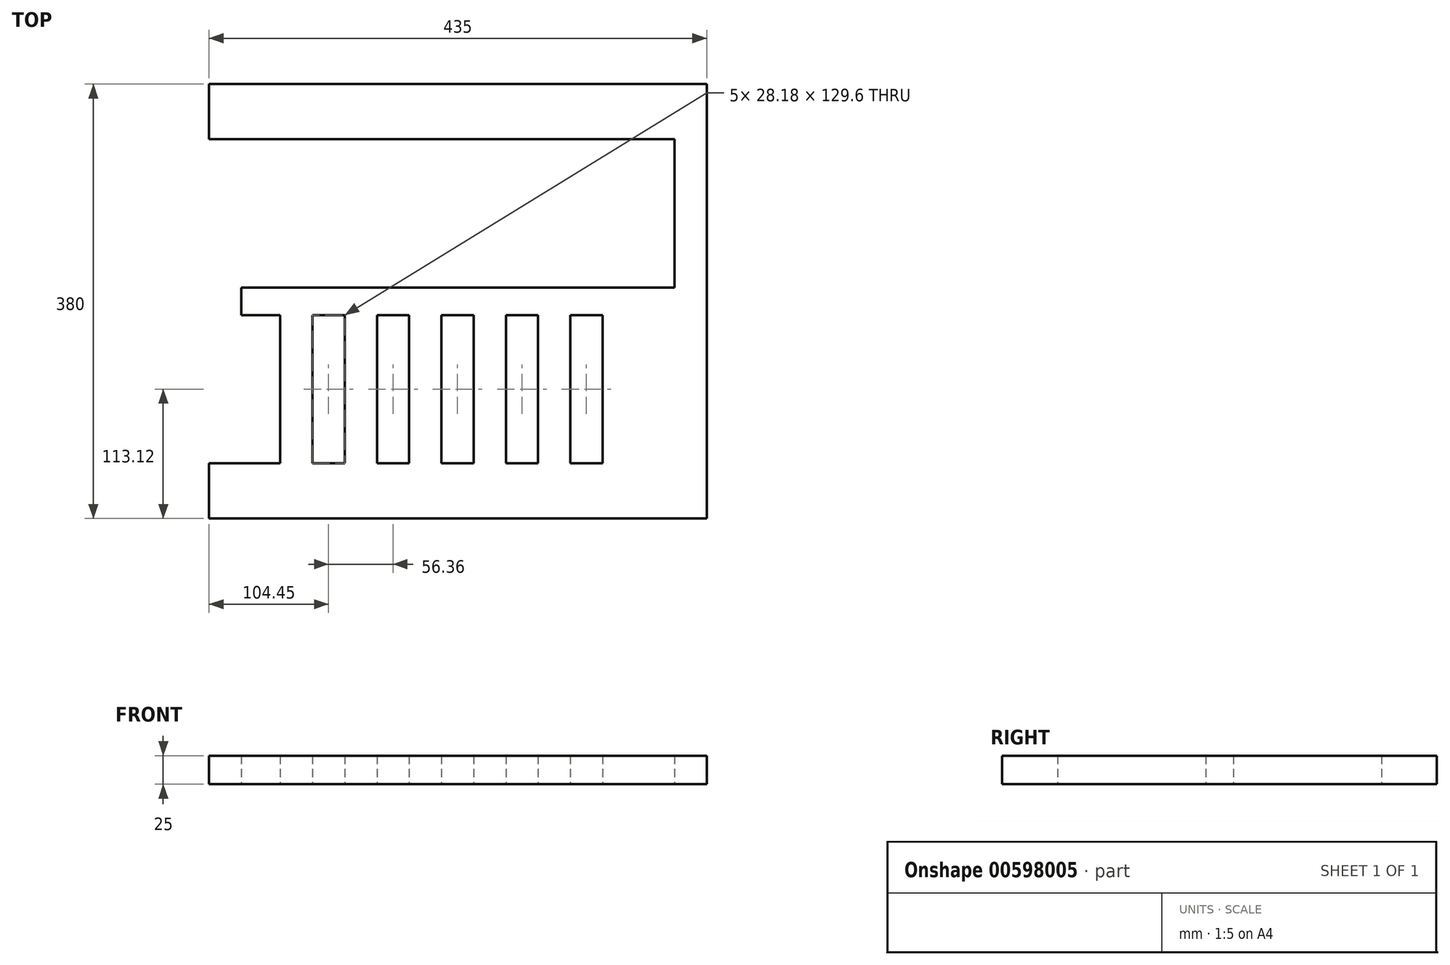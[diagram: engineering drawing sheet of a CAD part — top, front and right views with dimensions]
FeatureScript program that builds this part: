
annotation { "Feature Type Name" : "Feature", "Feature Type Description" : "" }
export const myFeature = defineFeature(function(context is Context, id is Id, definition is map)
    precondition{}
    {
        {
            var Q0;
            Q0=qCreatedBy(makeId("Top.planeOp"),FACE);
            var sketch = newSketch(context, id + "F0", { "sketchPlane" : qUnion([Q0])});
            skLineSegment(sketch, "E0.bottom", {"start": v(0, 0) * mm, "end": v(435, 0) * mm});
            skLineSegment(sketch, "E0.top", {"start": v(0, 380) * mm, "end": v(435, 380) * mm});
            skLineSegment(sketch, "E0.left", {"start": v(0, 0) * mm, "end": v(0, 380) * mm});
            skLineSegment(sketch, "E0.right", {"start": v(435, 0) * mm, "end": v(435, 380) * mm});
            skLineSegment(sketch, "E1", {"start": v(435, 0) * mm, "end": v(435, 48.32) * mm});
            skLineSegment(sketch, "E2", {"start": v(435, 380) * mm, "end": v(435, 331.68) * mm});
            skLineSegment(sketch, "E3.bottom", {"start": v(435, 331.68) * mm, "end": v(406.82, 331.68) * mm});
            skLineSegment(sketch, "E3.top", {"start": v(435, 48.32) * mm, "end": v(406.82, 48.32) * mm});
            skLineSegment(sketch, "E3.left", {"start": v(435, 331.68) * mm, "end": v(435, 48.32) * mm});
            skLineSegment(sketch, "E3.right", {"start": v(406.82, 331.68) * mm, "end": v(406.82, 48.32) * mm});
            skLineSegment(sketch, "E4", {"start": v(406.82, 331.68) * mm, "end": v(0, 331.68) * mm});
            skLineSegment(sketch, "E5", {"start": v(406.82, 48.32) * mm, "end": v(0, 48.32) * mm});
            skLineSegment(sketch, "E6.bottom", {"start": v(0, 331.68) * mm, "end": v(28.18, 331.68) * mm});
            skLineSegment(sketch, "E6.top", {"start": v(0, 48.32) * mm, "end": v(28.18, 48.32) * mm});
            skLineSegment(sketch, "E6.left", {"start": v(0, 331.68) * mm, "end": v(0, 48.32) * mm});
            skLineSegment(sketch, "E6.right", {"start": v(28.18, 331.68) * mm, "end": v(28.18, 48.32) * mm});
            skLineSegment(sketch, "E7", {"start": v(406.82, 48.32) * mm, "end": v(406.82, 177.92) * mm});
            skLineSegment(sketch, "E8", {"start": v(406.82, 331.68) * mm, "end": v(406.82, 202.08) * mm});
            skLineSegment(sketch, "E9", {"start": v(406.82, 202.08) * mm, "end": v(435, 202.08) * mm});
            skLineSegment(sketch, "E10", {"start": v(435, 177.75) * mm, "end": v(406.82, 177.92) * mm});
            skLineSegment(sketch, "E11", {"start": v(406.82, 202.08) * mm, "end": v(0, 202.08) * mm});
            skLineSegment(sketch, "E12", {"start": v(406.82, 177.92) * mm, "end": v(0, 177.92) * mm});
            skLineSegment(sketch, "E13", {"start": v(28.18, 331.68) * mm, "end": v(36.34, 331.68) * mm});
            skLineSegment(sketch, "E14", {"start": v(36.34, 331.68) * mm, "end": v(62.18, 331.68) * mm});
            skLineSegment(sketch, "E15", {"start": v(62.18, 331.68) * mm, "end": v(90.36, 331.68) * mm});
            skLineSegment(sketch, "E16", {"start": v(90.36, 331.68) * mm, "end": v(118.54, 331.68) * mm});
            skLineSegment(sketch, "E17", {"start": v(118.54, 331.68) * mm, "end": v(146.72, 331.68) * mm});
            skLineSegment(sketch, "E18", {"start": v(146.72, 331.68) * mm, "end": v(174.9, 331.68) * mm});
            skLineSegment(sketch, "E19", {"start": v(174.9, 331.68) * mm, "end": v(203.08, 331.68) * mm});
            skLineSegment(sketch, "E20", {"start": v(203.08, 331.68) * mm, "end": v(231.26, 331.68) * mm});
            skLineSegment(sketch, "E21", {"start": v(231.26, 331.68) * mm, "end": v(259.44, 331.68) * mm});
            skLineSegment(sketch, "E22", {"start": v(259.44, 331.68) * mm, "end": v(287.62, 331.68) * mm});
            skLineSegment(sketch, "E23", {"start": v(287.62, 331.68) * mm, "end": v(315.8, 331.68) * mm});
            skLineSegment(sketch, "E24", {"start": v(315.8, 331.68) * mm, "end": v(343.98, 331.68) * mm});
            skLineSegment(sketch, "E25", {"start": v(343.98, 331.68) * mm, "end": v(372.16, 331.68) * mm});
            skLineSegment(sketch, "E26", {"start": v(372.16, 331.68) * mm, "end": v(398.66, 331.68) * mm});
            skLineSegment(sketch, "E27", {"start": v(62.18, 331.68) * mm, "end": v(62.18, 48.32) * mm});
            skLineSegment(sketch, "E28", {"start": v(90.36, 331.68) * mm, "end": v(90.36, 48.32) * mm});
            skLineSegment(sketch, "E29", {"start": v(118.54, 331.68) * mm, "end": v(118.54, 48.32) * mm});
            skLineSegment(sketch, "E30", {"start": v(146.72, 331.68) * mm, "end": v(146.72, 48.32) * mm});
            skLineSegment(sketch, "E31", {"start": v(174.9, 331.68) * mm, "end": v(174.9, 48.32) * mm});
            skLineSegment(sketch, "E32", {"start": v(203.08, 331.68) * mm, "end": v(203.08, 48.32) * mm});
            skLineSegment(sketch, "E33", {"start": v(231.26, 331.68) * mm, "end": v(231.26, 48.32) * mm});
            skLineSegment(sketch, "E34", {"start": v(259.44, 331.68) * mm, "end": v(259.44, 48.32) * mm});
            skLineSegment(sketch, "E35", {"start": v(287.62, 331.68) * mm, "end": v(287.62, 48.32) * mm});
            skLineSegment(sketch, "E36", {"start": v(315.8, 331.68) * mm, "end": v(315.8, 48.32) * mm});
            skLineSegment(sketch, "E37", {"start": v(343.98, 331.68) * mm, "end": v(343.98, 48.32) * mm});
            skLineSegment(sketch, "E38", {"start": v(372.16, 331.68) * mm, "end": v(372.16, 48.32) * mm});
            skSolve(sketch);
        }
        {
            var Q0;
            {var subQ2=sQuery(id+"F0.wireOp",EDGE,"E0.top");Q0=makeQuery(id+"F0.imprint","IMPRINT",FACE,{"disambiguationData":[TD([[makeQuery(id+"F0.imprint","IMPRINT",EDGE,{"derivedFrom":subQ2}),-1.0]])]});}
            var Q1;
            {var subQ0=sQuery(id+"F0.wireOp",EDGE,"E6.bottom");Q1=makeQuery(id+"F0.imprint","IMPRINT",FACE,{"disambiguationData":[TD([[makeQuery(id+"F0.imprint","IMPRINT",EDGE,{"derivedFrom":subQ0}),-1.0]])]});}
            var Q2;
            {var subQ5=sQuery(id+"F0.wireOp",EDGE,"E15");Q2=makeQuery(id+"F0.imprint","IMPRINT",FACE,{"disambiguationData":[TD([[makeQuery(id+"F0.imprint","IMPRINT",EDGE,{"derivedFrom":subQ5}),-1.0]])]});}
            var Q3;
            {var subQ5=sQuery(id+"F0.wireOp",EDGE,"E17");Q3=makeQuery(id+"F0.imprint","IMPRINT",FACE,{"disambiguationData":[TD([[makeQuery(id+"F0.imprint","IMPRINT",EDGE,{"derivedFrom":subQ5}),-1.0]])]});}
            var Q4;
            {var subQ5=sQuery(id+"F0.wireOp",EDGE,"E19");Q4=makeQuery(id+"F0.imprint","IMPRINT",FACE,{"disambiguationData":[TD([[makeQuery(id+"F0.imprint","IMPRINT",EDGE,{"derivedFrom":subQ5}),-1.0]])]});}
            var Q5;
            {var subQ5=sQuery(id+"F0.wireOp",EDGE,"E21");Q5=makeQuery(id+"F0.imprint","IMPRINT",FACE,{"disambiguationData":[TD([[makeQuery(id+"F0.imprint","IMPRINT",EDGE,{"derivedFrom":subQ5}),-1.0]])]});}
            var Q6;
            {var subQ5=sQuery(id+"F0.wireOp",EDGE,"E23");Q6=makeQuery(id+"F0.imprint","IMPRINT",FACE,{"disambiguationData":[TD([[makeQuery(id+"F0.imprint","IMPRINT",EDGE,{"derivedFrom":subQ5}),-1.0]])]});}
            var Q7;
            {var subQ5=sQuery(id+"F0.wireOp",EDGE,"E25");Q7=makeQuery(id+"F0.imprint","IMPRINT",FACE,{"disambiguationData":[TD([[makeQuery(id+"F0.imprint","IMPRINT",EDGE,{"derivedFrom":subQ5}),-1.0]])]});}
            var Q8;
            {var subQ0=sQuery(id+"F0.wireOp",EDGE,"E3.bottom");Q8=makeQuery(id+"F0.imprint","IMPRINT",FACE,{"disambiguationData":[TD([[makeQuery(id+"F0.imprint","IMPRINT",EDGE,{"derivedFrom":subQ0}),1.0]])]});}
            var Q9;
            Q9=makeQuery(id+"F0.imprint","IMPRINT",FACE,{"disambiguationData":[TD([[makeQuery(id+"F0.imprint","IMPRINT",EDGE,{"derivedFrom":sQuery(id+"F0.wireOp",EDGE,"E3.right")}),1.0]])]});
            var Q10;
            {var subQ0=sQuery(id+"F0.wireOp",EDGE,"E3.right");Q10=makeQuery(id+"F0.imprint","IMPRINT",FACE,{"disambiguationData":[TD([[makeQuery(id+"F0.imprint","IMPRINT",EDGE,{"derivedFrom":subQ0}),-1.0]])]});}
            var Q11;
            {var subQ0=sQuery(id+"F0.wireOp",EDGE,"E38");var subQ1=sQuery(id+"F0.wireOp",EDGE,"E11");var subQ2=makeQuery(id+"F0.imprint","INTERSECT",VERTEX,{"derivedFrom":[subQ1,subQ0]});Q11=makeQuery(id+"F0.imprint","IMPRINT",FACE,{"disambiguationData":[TD([[makeQuery(id+"F0.imprint","IMPRINT",EDGE,{"disambiguationData":[TD([[subQ2,-1.0]])],"derivedFrom":subQ1}),1.0]])]});}
            var Q12;
            {var subQ0=sQuery(id+"F0.wireOp",EDGE,"E37");var subQ1=sQuery(id+"F0.wireOp",EDGE,"E11");var subQ2=makeQuery(id+"F0.imprint","INTERSECT",VERTEX,{"derivedFrom":[subQ1,subQ0]});Q12=makeQuery(id+"F0.imprint","IMPRINT",FACE,{"disambiguationData":[TD([[makeQuery(id+"F0.imprint","IMPRINT",EDGE,{"disambiguationData":[TD([[subQ2,-1.0]])],"derivedFrom":subQ1}),1.0]])]});}
            var Q13;
            {var subQ0=sQuery(id+"F0.wireOp",EDGE,"E36");var subQ1=sQuery(id+"F0.wireOp",EDGE,"E11");var subQ2=makeQuery(id+"F0.imprint","INTERSECT",VERTEX,{"derivedFrom":[subQ1,subQ0]});Q13=makeQuery(id+"F0.imprint","IMPRINT",FACE,{"disambiguationData":[TD([[makeQuery(id+"F0.imprint","IMPRINT",EDGE,{"disambiguationData":[TD([[subQ2,-1.0]])],"derivedFrom":subQ1}),1.0]])]});}
            var Q14;
            {var subQ0=sQuery(id+"F0.wireOp",EDGE,"E35");var subQ1=sQuery(id+"F0.wireOp",EDGE,"E11");var subQ2=makeQuery(id+"F0.imprint","INTERSECT",VERTEX,{"derivedFrom":[subQ1,subQ0]});Q14=makeQuery(id+"F0.imprint","IMPRINT",FACE,{"disambiguationData":[TD([[makeQuery(id+"F0.imprint","IMPRINT",EDGE,{"disambiguationData":[TD([[subQ2,-1.0]])],"derivedFrom":subQ1}),1.0]])]});}
            var Q15;
            {var subQ0=sQuery(id+"F0.wireOp",EDGE,"E34");var subQ1=sQuery(id+"F0.wireOp",EDGE,"E11");var subQ2=makeQuery(id+"F0.imprint","INTERSECT",VERTEX,{"derivedFrom":[subQ1,subQ0]});Q15=makeQuery(id+"F0.imprint","IMPRINT",FACE,{"disambiguationData":[TD([[makeQuery(id+"F0.imprint","IMPRINT",EDGE,{"disambiguationData":[TD([[subQ2,-1.0]])],"derivedFrom":subQ1}),1.0]])]});}
            var Q16;
            {var subQ0=sQuery(id+"F0.wireOp",EDGE,"E33");var subQ1=sQuery(id+"F0.wireOp",EDGE,"E11");var subQ2=makeQuery(id+"F0.imprint","INTERSECT",VERTEX,{"derivedFrom":[subQ1,subQ0]});Q16=makeQuery(id+"F0.imprint","IMPRINT",FACE,{"disambiguationData":[TD([[makeQuery(id+"F0.imprint","IMPRINT",EDGE,{"disambiguationData":[TD([[subQ2,-1.0]])],"derivedFrom":subQ1}),1.0]])]});}
            var Q17;
            {var subQ0=sQuery(id+"F0.wireOp",EDGE,"E32");var subQ1=sQuery(id+"F0.wireOp",EDGE,"E11");var subQ2=makeQuery(id+"F0.imprint","INTERSECT",VERTEX,{"derivedFrom":[subQ1,subQ0]});Q17=makeQuery(id+"F0.imprint","IMPRINT",FACE,{"disambiguationData":[TD([[makeQuery(id+"F0.imprint","IMPRINT",EDGE,{"disambiguationData":[TD([[subQ2,-1.0]])],"derivedFrom":subQ1}),1.0]])]});}
            var Q18;
            {var subQ0=sQuery(id+"F0.wireOp",EDGE,"E31");var subQ1=sQuery(id+"F0.wireOp",EDGE,"E11");var subQ2=makeQuery(id+"F0.imprint","INTERSECT",VERTEX,{"derivedFrom":[subQ1,subQ0]});Q18=makeQuery(id+"F0.imprint","IMPRINT",FACE,{"disambiguationData":[TD([[makeQuery(id+"F0.imprint","IMPRINT",EDGE,{"disambiguationData":[TD([[subQ2,-1.0]])],"derivedFrom":subQ1}),1.0]])]});}
            var Q19;
            {var subQ0=sQuery(id+"F0.wireOp",EDGE,"E30");var subQ1=sQuery(id+"F0.wireOp",EDGE,"E11");var subQ2=makeQuery(id+"F0.imprint","INTERSECT",VERTEX,{"derivedFrom":[subQ1,subQ0]});Q19=makeQuery(id+"F0.imprint","IMPRINT",FACE,{"disambiguationData":[TD([[makeQuery(id+"F0.imprint","IMPRINT",EDGE,{"disambiguationData":[TD([[subQ2,-1.0]])],"derivedFrom":subQ1}),1.0]])]});}
            var Q20;
            {var subQ0=sQuery(id+"F0.wireOp",EDGE,"E29");var subQ1=sQuery(id+"F0.wireOp",EDGE,"E11");var subQ2=makeQuery(id+"F0.imprint","INTERSECT",VERTEX,{"derivedFrom":[subQ1,subQ0]});Q20=makeQuery(id+"F0.imprint","IMPRINT",FACE,{"disambiguationData":[TD([[makeQuery(id+"F0.imprint","IMPRINT",EDGE,{"disambiguationData":[TD([[subQ2,-1.0]])],"derivedFrom":subQ1}),1.0]])]});}
            var Q21;
            {var subQ0=sQuery(id+"F0.wireOp",EDGE,"E28");var subQ1=sQuery(id+"F0.wireOp",EDGE,"E11");var subQ2=makeQuery(id+"F0.imprint","INTERSECT",VERTEX,{"derivedFrom":[subQ1,subQ0]});Q21=makeQuery(id+"F0.imprint","IMPRINT",FACE,{"disambiguationData":[TD([[makeQuery(id+"F0.imprint","IMPRINT",EDGE,{"disambiguationData":[TD([[subQ2,-1.0]])],"derivedFrom":subQ1}),1.0]])]});}
            var Q22;
            {var subQ0=sQuery(id+"F0.wireOp",EDGE,"E11");var subQ1=sQuery(id+"F0.wireOp",EDGE,"E6.right");var subQ2=makeQuery(id+"F0.imprint","INTERSECT",VERTEX,{"derivedFrom":[subQ1,subQ0]});Q22=makeQuery(id+"F0.imprint","IMPRINT",FACE,{"disambiguationData":[TD([[makeQuery(id+"F0.imprint","IMPRINT",EDGE,{"disambiguationData":[TD([[subQ2,-1.0]])],"derivedFrom":subQ1}),1.0]])]});}
            var Q23;
            {var subQ0=sQuery(id+"F0.wireOp",EDGE,"E11");var subQ1=sQuery(id+"F0.wireOp",EDGE,"E6.left");var subQ2=makeQuery(id+"F0.imprint","INTERSECT",VERTEX,{"derivedFrom":[subQ1,subQ0]});Q23=makeQuery(id+"F0.imprint","IMPRINT",FACE,{"disambiguationData":[TD([[makeQuery(id+"F0.imprint","IMPRINT",EDGE,{"disambiguationData":[TD([[subQ2,-1.0]])],"derivedFrom":subQ1}),1.0]])]});}
            var Q24;
            {var subQ0=sQuery(id+"F0.wireOp",EDGE,"E6.top");Q24=makeQuery(id+"F0.imprint","IMPRINT",FACE,{"disambiguationData":[TD([[makeQuery(id+"F0.imprint","IMPRINT",EDGE,{"derivedFrom":subQ0}),1.0]])]});}
            var Q25;
            {var subQ0=sQuery(id+"F0.wireOp",EDGE,"E27");var subQ1=sQuery(id+"F0.wireOp",EDGE,"E5");var subQ2=makeQuery(id+"F0.imprint","INTERSECT",VERTEX,{"derivedFrom":[subQ1,subQ0]});Q25=makeQuery(id+"F0.imprint","IMPRINT",FACE,{"disambiguationData":[TD([[makeQuery(id+"F0.imprint","IMPRINT",EDGE,{"disambiguationData":[TD([[subQ2,1.0]])],"derivedFrom":subQ1}),-1.0]])]});}
            var Q26;
            {var subQ0=sQuery(id+"F0.wireOp",EDGE,"E29");var subQ1=sQuery(id+"F0.wireOp",EDGE,"E5");var subQ2=makeQuery(id+"F0.imprint","INTERSECT",VERTEX,{"derivedFrom":[subQ1,subQ0]});Q26=makeQuery(id+"F0.imprint","IMPRINT",FACE,{"disambiguationData":[TD([[makeQuery(id+"F0.imprint","IMPRINT",EDGE,{"disambiguationData":[TD([[subQ2,1.0]])],"derivedFrom":subQ1}),-1.0]])]});}
            var Q27;
            {var subQ0=sQuery(id+"F0.wireOp",EDGE,"E31");var subQ1=sQuery(id+"F0.wireOp",EDGE,"E5");var subQ2=makeQuery(id+"F0.imprint","INTERSECT",VERTEX,{"derivedFrom":[subQ1,subQ0]});Q27=makeQuery(id+"F0.imprint","IMPRINT",FACE,{"disambiguationData":[TD([[makeQuery(id+"F0.imprint","IMPRINT",EDGE,{"disambiguationData":[TD([[subQ2,1.0]])],"derivedFrom":subQ1}),-1.0]])]});}
            var Q28;
            {var subQ0=sQuery(id+"F0.wireOp",EDGE,"E33");var subQ1=sQuery(id+"F0.wireOp",EDGE,"E5");var subQ2=makeQuery(id+"F0.imprint","INTERSECT",VERTEX,{"derivedFrom":[subQ1,subQ0]});Q28=makeQuery(id+"F0.imprint","IMPRINT",FACE,{"disambiguationData":[TD([[makeQuery(id+"F0.imprint","IMPRINT",EDGE,{"disambiguationData":[TD([[subQ2,1.0]])],"derivedFrom":subQ1}),-1.0]])]});}
            var Q29;
            {var subQ0=sQuery(id+"F0.wireOp",EDGE,"E35");var subQ1=sQuery(id+"F0.wireOp",EDGE,"E5");var subQ2=makeQuery(id+"F0.imprint","INTERSECT",VERTEX,{"derivedFrom":[subQ1,subQ0]});Q29=makeQuery(id+"F0.imprint","IMPRINT",FACE,{"disambiguationData":[TD([[makeQuery(id+"F0.imprint","IMPRINT",EDGE,{"disambiguationData":[TD([[subQ2,1.0]])],"derivedFrom":subQ1}),-1.0]])]});}
            var Q30;
            {var subQ0=sQuery(id+"F0.wireOp",EDGE,"E37");var subQ1=sQuery(id+"F0.wireOp",EDGE,"E5");var subQ2=makeQuery(id+"F0.imprint","INTERSECT",VERTEX,{"derivedFrom":[subQ1,subQ0]});Q30=makeQuery(id+"F0.imprint","IMPRINT",FACE,{"disambiguationData":[TD([[makeQuery(id+"F0.imprint","IMPRINT",EDGE,{"disambiguationData":[TD([[subQ2,1.0]])],"derivedFrom":subQ1}),-1.0]])]});}
            var Q31;
            {var subQ0=sQuery(id+"F0.wireOp",EDGE,"E3.top");Q31=makeQuery(id+"F0.imprint","IMPRINT",FACE,{"disambiguationData":[TD([[makeQuery(id+"F0.imprint","IMPRINT",EDGE,{"derivedFrom":subQ0}),-1.0]])]});}
            var Q32;
            {var subQ6=sQuery(id+"F0.wireOp",EDGE,"E0.bottom");Q32=makeQuery(id+"F0.imprint","IMPRINT",FACE,{"disambiguationData":[TD([[makeQuery(id+"F0.imprint","IMPRINT",EDGE,{"derivedFrom":subQ6}),1.0]])]});}
            extrude(context, id + "F1", {"entities" : qUnion([Q0, Q1, Q2, Q3, Q4, Q5, Q6, Q7, Q8, Q9, Q10, Q11, Q12, Q13, Q14, Q15, Q16, Q17, Q18, Q19, Q20, Q21, Q22, Q23, Q24, Q25, Q26, Q27, Q28, Q29, Q30, Q31, Q32]), "depth" : 25 * mm, "offsetDistance" : 25 * mm});
        }
    });
